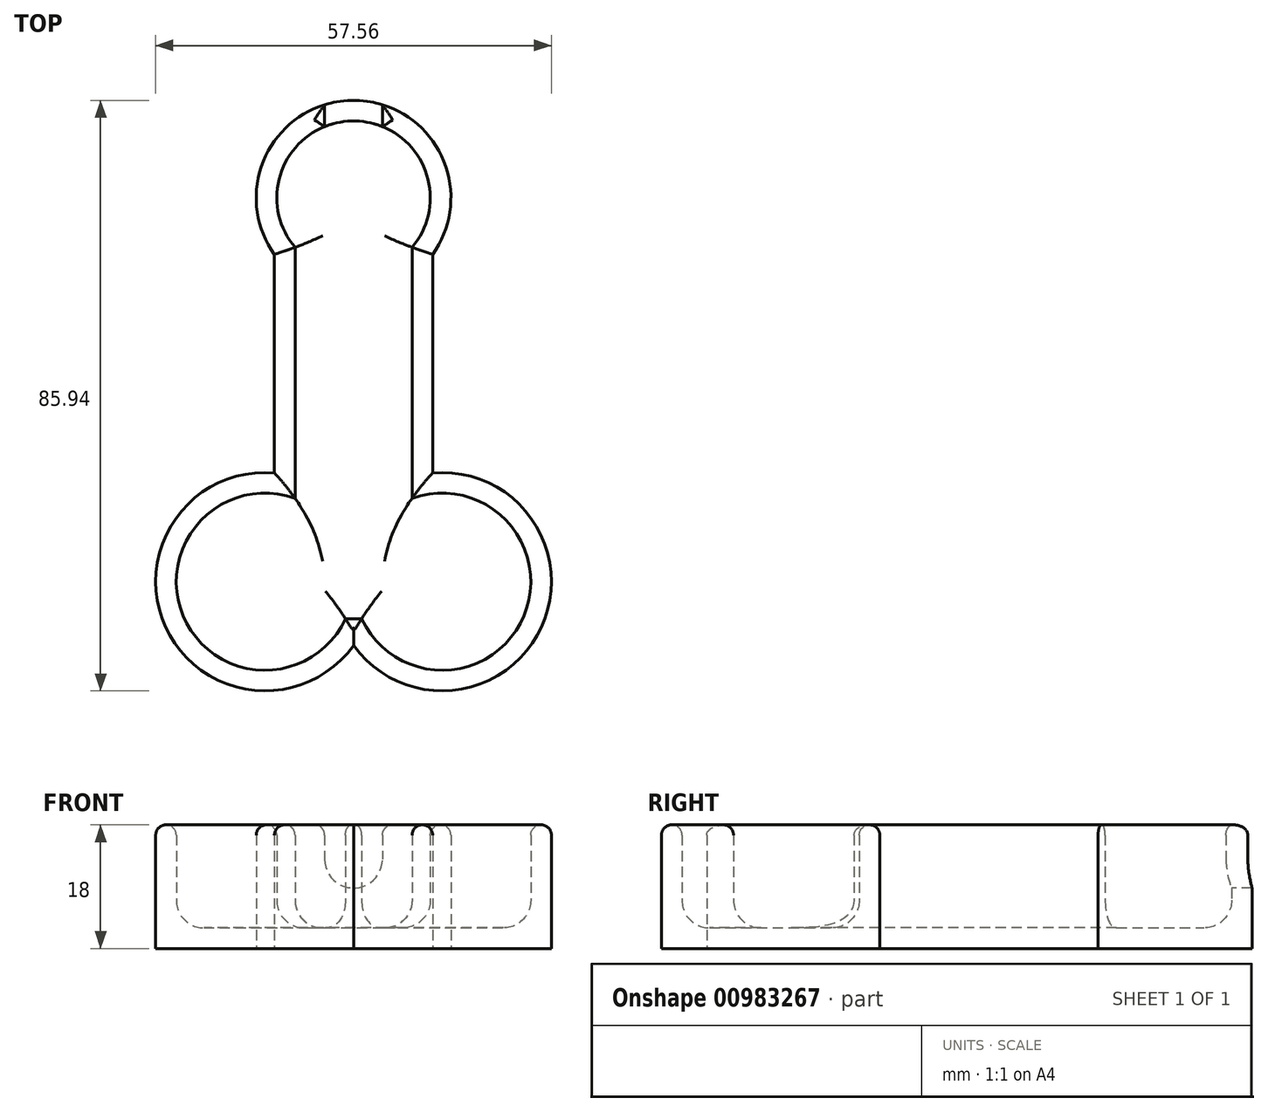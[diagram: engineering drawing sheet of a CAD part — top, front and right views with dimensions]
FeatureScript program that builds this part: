
annotation { "Feature Type Name" : "Feature", "Feature Type Description" : "" }
export const myFeature = defineFeature(function(context is Context, id is Id, definition is map)
    precondition{}
    {
        {
            var Q0;
            Q0=qCreatedBy(makeId("Top.planeOp"),FACE);
            var sketch = newSketch(context, id + "F0", { "sketchPlane" : qUnion([Q0])});
            skCircle(sketch, "E0", {"center": v(-12.9, 0) * mm, "radius": 12.9 * mm});
            skCircle(sketch, "E1", {"center": v(12.9, 0) * mm, "radius": 12.9 * mm});
            skLineSegment(sketch, "E2.bottom", {"start": v(8.51, 55.89) * mm, "end": v(-8.51, 55.89) * mm});
            skLineSegment(sketch, "E2.top", {"start": v(8.51, 0) * mm, "end": v(-8.51, 0) * mm});
            skLineSegment(sketch, "E2.left", {"start": v(8.51, 55.89) * mm, "end": v(8.51, 0) * mm});
            skLineSegment(sketch, "E2.right", {"start": v(-8.51, 55.89) * mm, "end": v(-8.51, 0) * mm});
            skPoint(sketch, "E2.middle", {"position": v(0, 27.94) * mm});
            skCircle(sketch, "E3", {"center": v(0, 55.89) * mm, "radius": 11.16 * mm});
            skLineSegment(sketch, "E4.bottom", {"start": v(-8.51, 0) * mm, "end": v(8.51, 0) * mm});
            skLineSegment(sketch, "E4.top", {"start": v(-8.51, -5.4) * mm, "end": v(8.51, -5.4) * mm});
            skLineSegment(sketch, "E4.left", {"start": v(-8.51, 0) * mm, "end": v(-8.51, -5.4) * mm});
            skLineSegment(sketch, "E4.right", {"start": v(8.51, 0) * mm, "end": v(8.51, -5.4) * mm});
            skSolve(sketch);
        }
        {
            var Q0;
            {var subQ0=sQuery(id+"F0.wireOp",EDGE,"E2.bottom");Q0=makeQuery(id+"F0.imprint","IMPRINT",FACE,{"disambiguationData":[TD([[makeQuery(id+"F0.imprint","IMPRINT",EDGE,{"derivedFrom":subQ0}),-1.0]])]});}
            var Q1;
            {var subQ5=sQuery(id+"F0.wireOp",EDGE,"E1");var subQ7=sQuery(id+"F0.wireOp",EDGE,"E2.left");var subQ8=makeQuery(id+"F0.imprint","INTERSECT",VERTEX,{"derivedFrom":[subQ5,subQ7]});Q1=makeQuery(id+"F0.imprint","IMPRINT",FACE,{"disambiguationData":[TD([[makeQuery(id+"F0.imprint","IMPRINT",EDGE,{"disambiguationData":[TD([[subQ8,1.0]])],"derivedFrom":subQ7}),-1.0]])]});}
            var Q2;
            {var subQ0=sQuery(id+"F0.wireOp",EDGE,"E2.right");var subQ3=sQuery(id+"F0.wireOp",EDGE,"E2.top");var subQ5=makeQuery(id+"F0.imprint","INTERSECT",VERTEX,{"derivedFrom":[subQ3,subQ0]});Q2=makeQuery(id+"F0.imprint","IMPRINT",FACE,{"disambiguationData":[TD([[makeQuery(id+"F0.imprint","IMPRINT",EDGE,{"disambiguationData":[TD([[subQ5,1.0]])],"derivedFrom":subQ0}),-1.0]])]});}
            var Q3;
            {var subQ0=sQuery(id+"F0.wireOp",EDGE,"E2.left");var subQ3=sQuery(id+"F0.wireOp",EDGE,"E2.top");var subQ5=makeQuery(id+"F0.imprint","INTERSECT",VERTEX,{"derivedFrom":[subQ3,subQ0]});Q3=makeQuery(id+"F0.imprint","IMPRINT",FACE,{"disambiguationData":[TD([[makeQuery(id+"F0.imprint","IMPRINT",EDGE,{"disambiguationData":[TD([[subQ5,1.0]])],"derivedFrom":subQ0}),1.0]])]});}
            var Q4;
            {var subQ0=sQuery(id+"F0.wireOp",EDGE,"E2.right");var subQ3=sQuery(id+"F0.wireOp",EDGE,"E2.top");var subQ5=makeQuery(id+"F0.imprint","INTERSECT",VERTEX,{"derivedFrom":[subQ3,subQ0]});Q4=makeQuery(id+"F0.imprint","IMPRINT",FACE,{"disambiguationData":[TD([[makeQuery(id+"F0.imprint","IMPRINT",EDGE,{"disambiguationData":[TD([[subQ5,1.0]])],"derivedFrom":subQ0}),1.0]])]});}
            var Q5;
            {var subQ0=sQuery(id+"F0.wireOp",EDGE,"E2.left");var subQ3=sQuery(id+"F0.wireOp",EDGE,"E2.top");var subQ5=makeQuery(id+"F0.imprint","INTERSECT",VERTEX,{"derivedFrom":[subQ3,subQ0]});Q5=makeQuery(id+"F0.imprint","IMPRINT",FACE,{"disambiguationData":[TD([[makeQuery(id+"F0.imprint","IMPRINT",EDGE,{"disambiguationData":[TD([[subQ5,1.0]])],"derivedFrom":subQ0}),-1.0]])]});}
            var Q6;
            {var subQ0=sQuery(id+"F0.wireOp",EDGE,"E2.bottom");Q6=makeQuery(id+"F0.imprint","IMPRINT",FACE,{"disambiguationData":[TD([[makeQuery(id+"F0.imprint","IMPRINT",EDGE,{"derivedFrom":subQ0}),1.0]])]});}
            var Q7;
            {var subQ0=sQuery(id+"F0.wireOp",EDGE,"E2.right");var subQ1=sQuery(id+"F0.wireOp",EDGE,"E0");var subQ2=makeQuery(id+"F0.imprint","INTERSECT",VERTEX,{"derivedFrom":[subQ1,subQ0]});Q7=makeQuery(id+"F0.imprint","IMPRINT",FACE,{"disambiguationData":[TD([[makeQuery(id+"F0.imprint","IMPRINT",EDGE,{"disambiguationData":[TD([[subQ2,1.0]])],"derivedFrom":subQ1}),1.0]])]});}
            var Q8;
            {var subQ5=sQuery(id+"F0.wireOp",EDGE,"E4.left");Q8=makeQuery(id+"F0.imprint","IMPRINT",FACE,{"disambiguationData":[TD([[makeQuery(id+"F0.imprint","IMPRINT",EDGE,{"derivedFrom":subQ5}),1.0]])]});}
            var Q9;
            {var subQ0=sQuery(id+"F0.wireOp",EDGE,"E4.top");var subQ1=sQuery(id+"F0.wireOp",EDGE,"E0");var subQ2=makeQuery(id+"F0.imprint","INTERSECT",VERTEX,{"derivedFrom":[subQ1,subQ0]});Q9=makeQuery(id+"F0.imprint","IMPRINT",FACE,{"disambiguationData":[TD([[makeQuery(id+"F0.imprint","IMPRINT",EDGE,{"disambiguationData":[TD([[subQ2,-1.0]])],"derivedFrom":subQ0}),1.0]])]});}
            var Q10;
            {var subQ5=sQuery(id+"F0.wireOp",EDGE,"E4.right");Q10=makeQuery(id+"F0.imprint","IMPRINT",FACE,{"disambiguationData":[TD([[makeQuery(id+"F0.imprint","IMPRINT",EDGE,{"derivedFrom":subQ5}),-1.0]])]});}
            var Q11;
            {var subQ0=sQuery(id+"F0.wireOp",EDGE,"E2.left");var subQ1=sQuery(id+"F0.wireOp",EDGE,"E1");var subQ2=makeQuery(id+"F0.imprint","INTERSECT",VERTEX,{"derivedFrom":[subQ1,subQ0]});Q11=makeQuery(id+"F0.imprint","IMPRINT",FACE,{"disambiguationData":[TD([[makeQuery(id+"F0.imprint","IMPRINT",EDGE,{"disambiguationData":[TD([[subQ2,-1.0]])],"derivedFrom":subQ1}),1.0]])]});}
            var Q12;
            {var subQ5=sQuery(id+"F0.wireOp",EDGE,"E4.left");Q12=makeQuery(id+"F0.imprint","IMPRINT",FACE,{"disambiguationData":[TD([[makeQuery(id+"F0.imprint","IMPRINT",EDGE,{"derivedFrom":subQ5}),-1.0]])]});}
            var Q13;
            {var subQ5=sQuery(id+"F0.wireOp",EDGE,"E4.right");Q13=makeQuery(id+"F0.imprint","IMPRINT",FACE,{"disambiguationData":[TD([[makeQuery(id+"F0.imprint","IMPRINT",EDGE,{"derivedFrom":subQ5}),1.0]])]});}
            extrude(context, id + "F1", {"entities" : qUnion([Q0, Q1, Q2, Q3, Q4, Q5, Q6, Q7, Q8, Q9, Q10, Q11, Q12, Q13]), "depth" : 15 * mm, "offsetDistance" : 25 * mm});
        }
        {
            var Q0;
            Q0=makeQuery(id+"F1.opExtrude","CAP_FACE",FACE,{"disambiguationData":[OSD([sQuery(id+"F0.wireOp",EDGE,"E0"),sQuery(id+"F0.wireOp",EDGE,"E1"),sQuery(id+"F0.wireOp",EDGE,"E2.left"),sQuery(id+"F0.wireOp",EDGE,"E2.right"),sQuery(id+"F0.wireOp",EDGE,"E3"),sQuery(id+"F0.wireOp",EDGE,"E4.top")])],"isStart":false});
            var Q1;
            Q1=makeQuery(id+"F1.opExtrude","SWEPT_BODY",BODY,{"disambiguationData":[OSD([sQuery(id+"F0.wireOp",EDGE,"E0"),sQuery(id+"F0.wireOp",EDGE,"E1"),sQuery(id+"F0.wireOp",EDGE,"E2.left"),sQuery(id+"F0.wireOp",EDGE,"E2.right"),sQuery(id+"F0.wireOp",EDGE,"E3"),sQuery(id+"F0.wireOp",EDGE,"E4.top")])]});
            shell(context, id + "F2", {"entities" : qUnion([Q0]), "parts" : qUnion([Q1]), "thickness" : 3 * mm, "oppositeDirection" : true});
        }
        {
            var Q0;
            Q0=qCreatedBy(makeId("Front.planeOp"),FACE);
            var sketch = newSketch(context, id + "F3", { "sketchPlane" : qUnion([Q0])});
            skCircle(sketch, "E5", {"center": v(0, 10) * mm, "radius": 4.2 * mm});
            skLineSegment(sketch, "E6.bottom", {"start": v(4.2, 10) * mm, "end": v(-4.2, 10) * mm});
            skLineSegment(sketch, "E6.top", {"start": v(4.2, 25.37) * mm, "end": v(-4.2, 25.37) * mm});
            skLineSegment(sketch, "E6.left", {"start": v(4.2, 10) * mm, "end": v(4.2, 25.37) * mm});
            skLineSegment(sketch, "E6.right", {"start": v(-4.2, 10) * mm, "end": v(-4.2, 25.37) * mm});
            skSolve(sketch);
        }
        {
            var Q0;
            Q0=makeQuery(id+"F3.imprint","IMPRINT",FACE,{"disambiguationData":[TD([[makeQuery(id+"F3.imprint","IMPRINT",EDGE,{"derivedFrom":sQuery(id+"F3.wireOp",EDGE,"E5")}),1.0]])]});
            var Q1;
            Q1=makeQuery(id+"F3.imprint","IMPRINT",FACE,{"disambiguationData":[TD([[makeQuery(id+"F3.imprint","IMPRINT",EDGE,{"derivedFrom":sQuery(id+"F3.wireOp",EDGE,"E6.top")}),1.0]])]});
            extrude(context, id + "F4", {"entities" : qUnion([Q0, Q1]), "operationType" : NewBodyOperationType.REMOVE, "oppositeDirection" : true, "depth" : 87.3 * mm, "offsetDistance" : 25 * mm});
        }
        {
            var Q0;
            {var subQ0=sQuery(id+"F0.wireOp",EDGE,"E4.top");var subQ1=sQuery(id+"F0.wireOp",EDGE,"E3");var subQ2=sQuery(id+"F0.wireOp",EDGE,"E2.right");var subQ3=sQuery(id+"F0.wireOp",EDGE,"E2.left");var subQ4=sQuery(id+"F0.wireOp",EDGE,"E1");var subQ5=sQuery(id+"F0.wireOp",EDGE,"E0");Q0=makeQuery(id+"F2.opShell","OFFSET_FACE",FACE,{"disambiguationData":[OSD([subQ5,subQ4,subQ3,subQ2,subQ1,subQ0]),TDD([makeQuery(id+"F1.opExtrude","CAP_FACE",FACE,{"disambiguationData":[OSD([subQ5,subQ4,subQ3,subQ2,subQ1,subQ0])],"isStart":true})])]});}
            fillet(context, id + "F5", {"entities" : qUnion([Q0]), "radius" : 4 * mm, "tangentPropagation" : true, "allowEdgeOverflow" : false});
        }
        {
            var Q0;
            Q0=makeQuery(id+"F1.opExtrude","CAP_FACE",FACE,{"disambiguationData":[OSD([sQuery(id+"F0.wireOp",EDGE,"E0"),sQuery(id+"F0.wireOp",EDGE,"E1"),sQuery(id+"F0.wireOp",EDGE,"E2.left"),sQuery(id+"F0.wireOp",EDGE,"E2.right"),sQuery(id+"F0.wireOp",EDGE,"E3"),sQuery(id+"F0.wireOp",EDGE,"E4.top")])],"isStart":false});
            fillet(context, id + "F6", {"entities" : qUnion([Q0]), "radius" : 1.5 * mm, "tangentPropagation" : true, "allowEdgeOverflow" : false});
        }
    });
